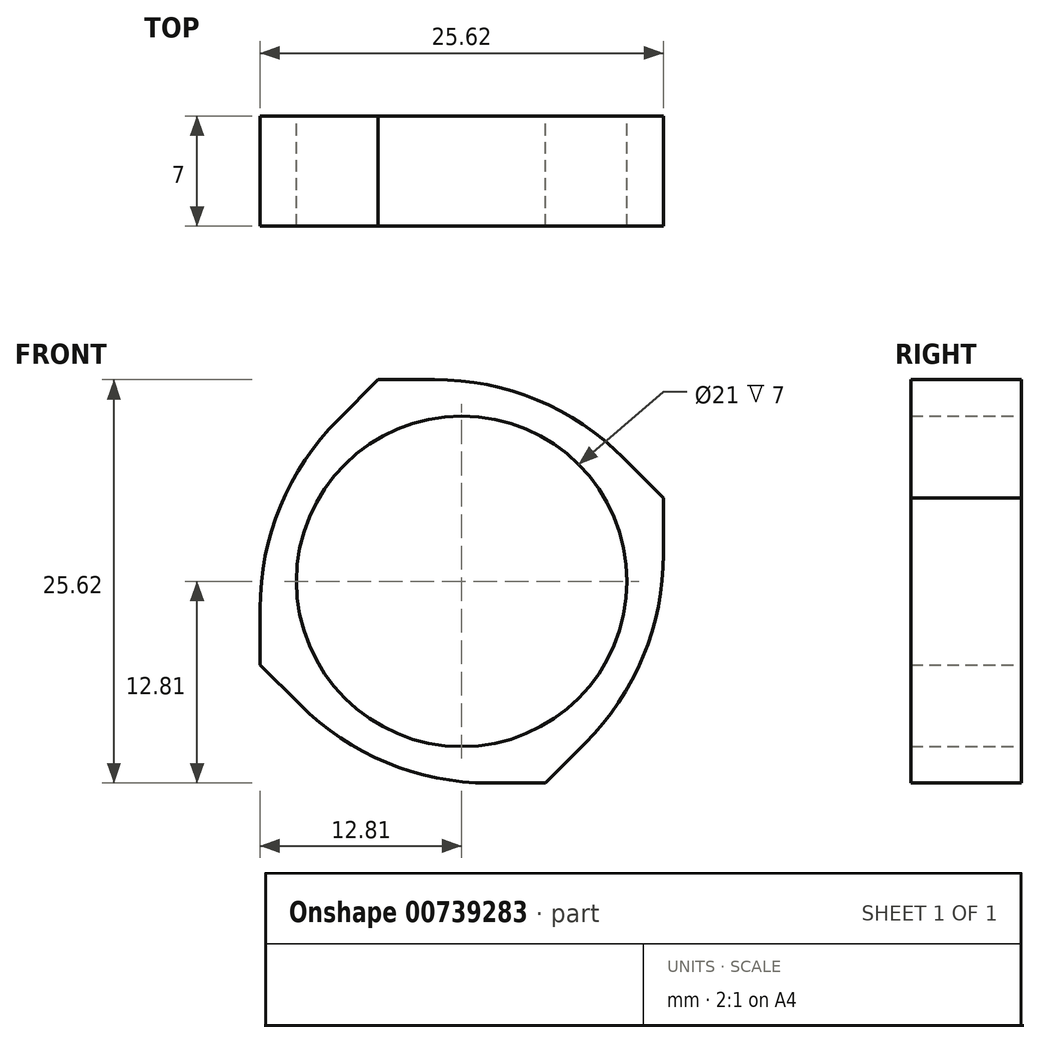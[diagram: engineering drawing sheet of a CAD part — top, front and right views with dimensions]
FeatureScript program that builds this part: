
annotation { "Feature Type Name" : "Feature", "Feature Type Description" : "" }
export const myFeature = defineFeature(function(context is Context, id is Id, definition is map)
    precondition{}
    {
        {
            var Q0;
            Q0=qCreatedBy(makeId("Front.planeOp"),FACE);
            var sketch = newSketch(context, id + "F0", { "sketchPlane" : qUnion([Q0])});
            skCircle(sketch, "E0", {"center": v(0, 0) * mm, "radius": 10.5 * mm});
            skCircle(sketch, "E1.cCircle", {"center": v(0, 0) * mm, "radius": 12.81 * mm, "construction": true});
            skLineSegment(sketch, "E1.0", {"start": v(5.3, -12.81) * mm, "end": v(-5.3, -12.81) * mm});
            skLineSegment(sketch, "E1.1", {"start": v(-5.3, -12.81) * mm, "end": v(-12.81, -5.3) * mm});
            skLineSegment(sketch, "E1.2", {"start": v(-12.81, -5.3) * mm, "end": v(-12.81, 5.3) * mm});
            skLineSegment(sketch, "E1.3", {"start": v(-12.81, 5.3) * mm, "end": v(-5.3, 12.81) * mm});
            skLineSegment(sketch, "E1.4", {"start": v(-5.3, 12.81) * mm, "end": v(5.3, 12.81) * mm});
            skLineSegment(sketch, "E1.5", {"start": v(5.3, 12.81) * mm, "end": v(12.81, 5.3) * mm});
            skLineSegment(sketch, "E1.6", {"start": v(12.81, 5.3) * mm, "end": v(12.81, -5.3) * mm});
            skLineSegment(sketch, "E1.7", {"start": v(12.81, -5.3) * mm, "end": v(5.3, -12.81) * mm});
            skPoint(sketch, "E1.0.midPoint", {"position": v(0, -12.81) * mm});
            skSolve(sketch);
        }
        {
            var Q0;
            Q0=qSketchRegion(id+"F0",true);
            extrude(context, id + "F1", {"entities" : qUnion([Q0]), "depth" : 7 * mm, "offsetDistance" : 25 * mm});
        }
        {
            var Q0;
            Q0=makeQuery(id+"F1.opExtrude","SWEPT_EDGE",EDGE,{"disambiguationData":[OSD([sQuery(id+"F0.wireOp",EDGE,"E1.2"),sQuery(id+"F0.wireOp",EDGE,"E1.3")])]});
            var Q1;
            Q1=makeQuery(id+"F1.opExtrude","SWEPT_EDGE",EDGE,{"disambiguationData":[OSD([sQuery(id+"F0.wireOp",EDGE,"E1.4"),sQuery(id+"F0.wireOp",EDGE,"E1.5")])]});
            var Q2;
            Q2=makeQuery(id+"F1.opExtrude","SWEPT_EDGE",EDGE,{"disambiguationData":[OSD([sQuery(id+"F0.wireOp",EDGE,"E1.6"),sQuery(id+"F0.wireOp",EDGE,"E1.7")])]});
            var Q3;
            Q3=makeQuery(id+"F1.opExtrude","SWEPT_EDGE",EDGE,{"disambiguationData":[OSD([sQuery(id+"F0.wireOp",EDGE,"E1.0"),sQuery(id+"F0.wireOp",EDGE,"E1.1")])]});
            fillet(context, id + "F2", {"entities" : qUnion([Q0, Q1, Q2, Q3]), "radius" : 17 * mm, "tangentPropagation" : true, "allowEdgeOverflow" : false});
        }
    });
